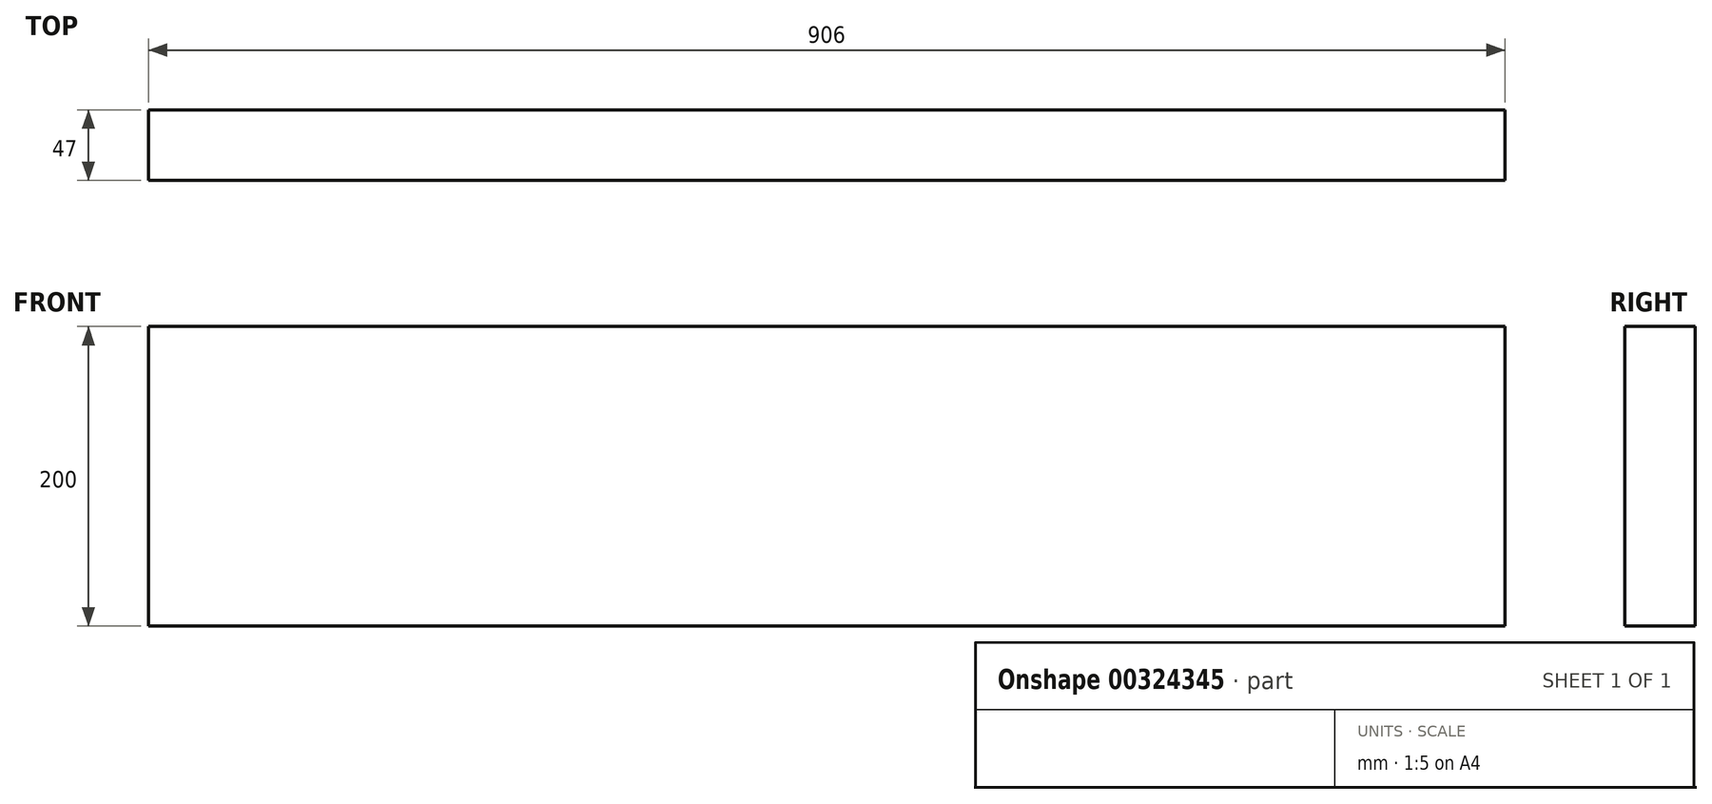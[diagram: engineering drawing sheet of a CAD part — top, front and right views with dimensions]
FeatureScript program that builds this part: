
annotation { "Feature Type Name" : "Feature", "Feature Type Description" : "" }
export const myFeature = defineFeature(function(context is Context, id is Id, definition is map)
    precondition{}
    {
        {
            var Q0;
            Q0=qCreatedBy(makeId("Top.planeOp"),FACE);
            var sketch = newSketch(context, id + "F0", { "sketchPlane" : qUnion([Q0])});
            skLineSegment(sketch, "E0.bottom", {"start": v(453, -23.5) * mm, "end": v(-453, -23.5) * mm});
            skLineSegment(sketch, "E0.top", {"start": v(453, 23.5) * mm, "end": v(-453, 23.5) * mm});
            skLineSegment(sketch, "E0.left", {"start": v(453, -23.5) * mm, "end": v(453, 23.5) * mm});
            skLineSegment(sketch, "E0.right", {"start": v(-453, -23.5) * mm, "end": v(-453, 23.5) * mm});
            skPoint(sketch, "E0.middle", {"position": v(0, 0) * mm});
            skSolve(sketch);
        }
        {
            var Q0;
            Q0=makeQuery(id+"F0.imprint","IMPRINT",FACE,{"disambiguationData":[TD([[makeQuery(id+"F0.imprint","IMPRINT",EDGE,{"derivedFrom":sQuery(id+"F0.wireOp",EDGE,"E0.bottom")}),-1.0]])]});
            extrude(context, id + "F1", {"entities" : qUnion([Q0]), "depth" : 200 * mm});
        }
    });
